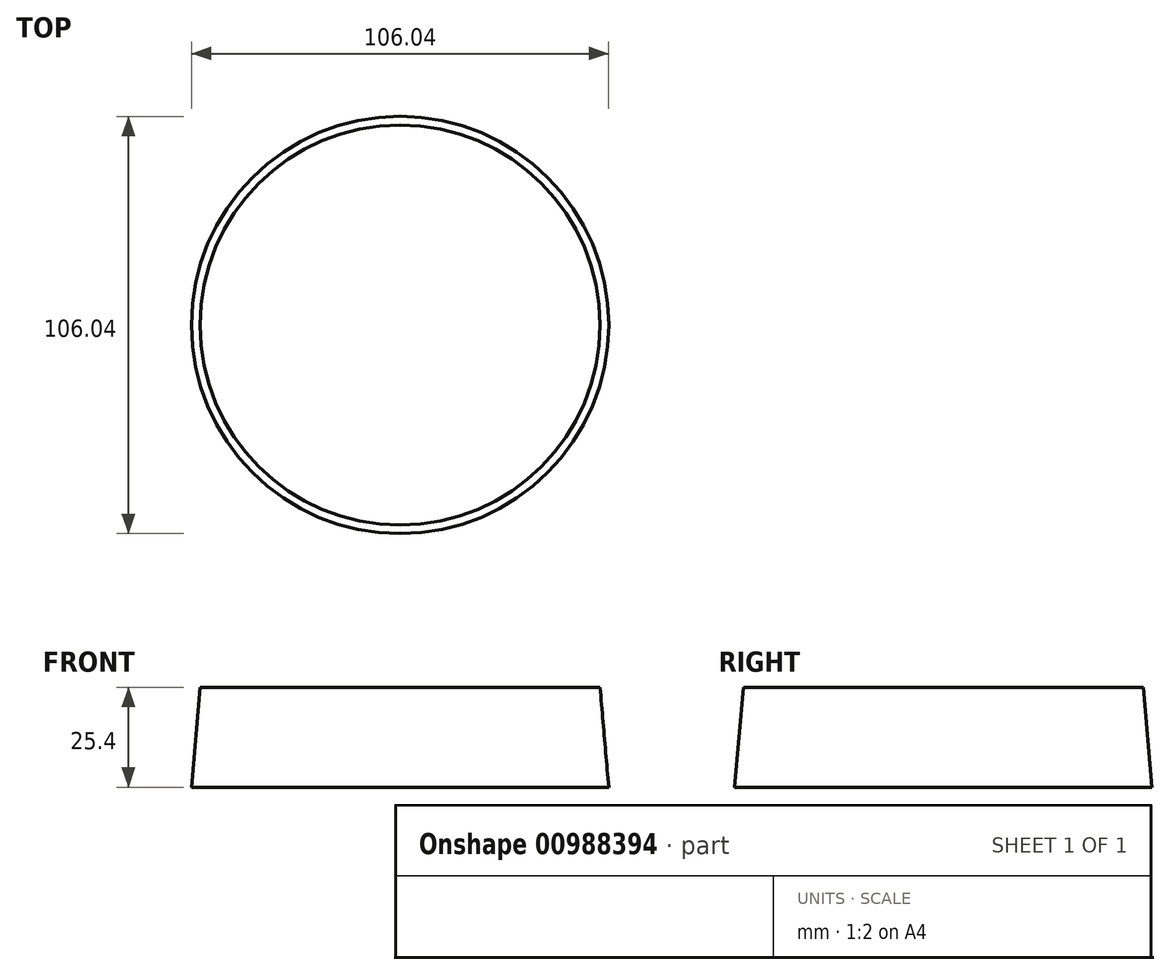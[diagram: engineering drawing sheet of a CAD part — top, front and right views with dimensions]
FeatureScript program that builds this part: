
annotation { "Feature Type Name" : "Feature", "Feature Type Description" : "" }
export const myFeature = defineFeature(function(context is Context, id is Id, definition is map)
    precondition{}
    {
        {
            var Q0;
            Q0=qCreatedBy(makeId("Front.planeOp"),FACE);
            var sketch = newSketch(context, id + "F0", { "sketchPlane" : qUnion([Q0])});
            skLineSegment(sketch, "E0", {"start": v(0, 0) * mm, "end": v(53.02, 0) * mm});
            skLineSegment(sketch, "E1", {"start": v(53.02, 0) * mm, "end": v(50.8, 25.4) * mm});
            skLineSegment(sketch, "E2", {"start": v(50.8, 25.4) * mm, "end": v(0, 25.4) * mm});
            skLineSegment(sketch, "E3", {"start": v(0, 25.4) * mm, "end": v(0, 0) * mm});
            skSolve(sketch);
        }
        {
            var Q0;
            Q0=makeQuery(id+"F0.imprint","IMPRINT",FACE,{"disambiguationData":[TD([[makeQuery(id+"F0.imprint","IMPRINT",EDGE,{"derivedFrom":sQuery(id+"F0.wireOp",EDGE,"E0")}),1.0]])]});
            var Q1;
            Q1=sQuery(id+"F0.wireOp",EDGE,"E3");
            revolve(context, id + "F1", {"surfaceOperationType" : NewSurfaceOperationType.NEW, "entities" : qUnion([Q0]), "axis" : qUnion([Q1]), "revolveType" : RevolveType.FULL});
        }
    });
